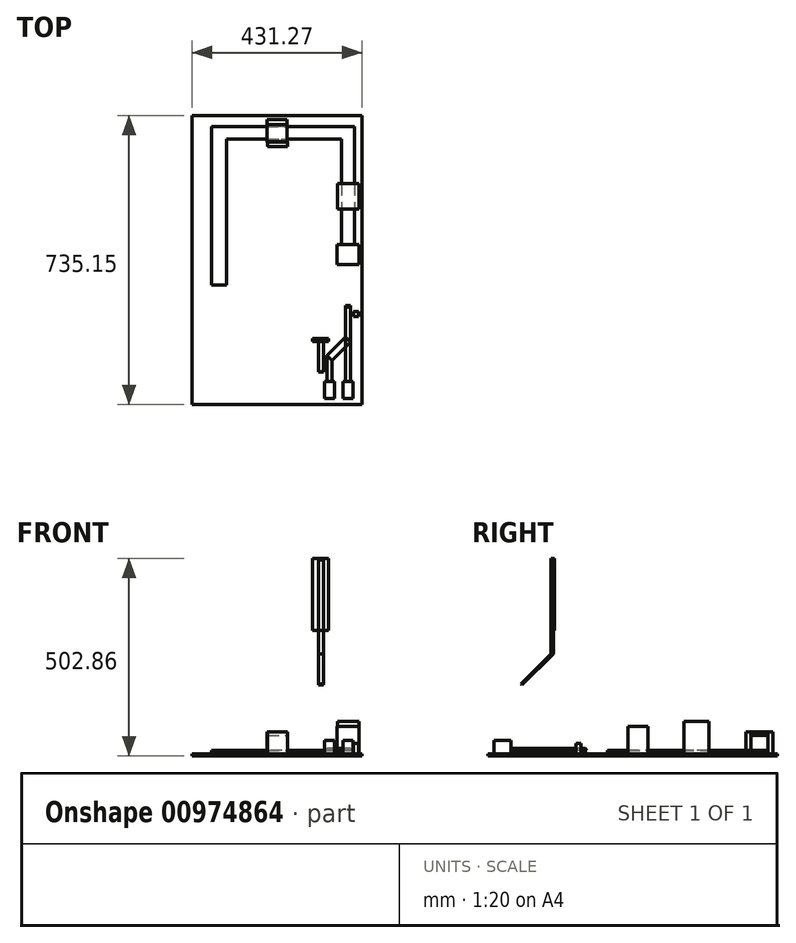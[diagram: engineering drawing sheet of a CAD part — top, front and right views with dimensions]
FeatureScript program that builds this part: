
annotation { "Feature Type Name" : "Feature", "Feature Type Description" : "" }
export const myFeature = defineFeature(function(context is Context, id is Id, definition is map)
    precondition{}
    {
        {
            var Q0;
            Q0=qCreatedBy(makeId("Top.planeOp"),FACE);
            var sketch = newSketch(context, id + "F0", { "sketchPlane" : qUnion([Q0])});
            skLineSegment(sketch, "E0.bottom", {"start": v(-24.86, -13.92) * mm, "end": v(0.54, -13.92) * mm});
            skLineSegment(sketch, "E0.top", {"start": v(-24.86, -57.1) * mm, "end": v(0.54, -57.1) * mm});
            skLineSegment(sketch, "E0.left", {"start": v(-24.86, -13.92) * mm, "end": v(-24.86, -57.1) * mm});
            skLineSegment(sketch, "E0.right", {"start": v(0.54, -13.92) * mm, "end": v(0.54, -57.1) * mm});
            skLineSegment(sketch, "E1.bottom", {"start": v(21.67, -13.98) * mm, "end": v(47.07, -13.98) * mm});
            skLineSegment(sketch, "E1.top", {"start": v(21.67, -57.16) * mm, "end": v(47.07, -57.16) * mm});
            skLineSegment(sketch, "E1.left", {"start": v(21.67, -13.98) * mm, "end": v(21.67, -57.16) * mm});
            skLineSegment(sketch, "E1.right", {"start": v(47.07, -13.98) * mm, "end": v(47.07, -57.16) * mm});
            skSolve(sketch);
        }
        {
            var Q0;
            Q0=qSketchRegion(id+"F0",true);
            extrude(context, id + "F1", {"entities" : qUnion([Q0]), "depth" : 34.3 * mm, "offsetDistance" : 25.4 * mm});
        }
        {
            var Q0;
            Q0=makeQuery(id+"F1.opExtrude","SWEPT_FACE",FACE,{"disambiguationData":[OSD([sQuery(id+"F0.wireOp",EDGE,"E1.bottom")])]});
            var sketch = newSketch(context, id + "F2", { "sketchPlane" : qUnion([Q0])});
            skLineSegment(sketch, "E2.bottom", {"start": v(-40.72, 13.97) * mm, "end": v(-28.02, 13.97) * mm});
            skLineSegment(sketch, "E2.top", {"start": v(-40.72, 9.52) * mm, "end": v(-28.02, 9.52) * mm});
            skLineSegment(sketch, "E2.left", {"start": v(-40.72, 13.97) * mm, "end": v(-40.72, 9.52) * mm});
            skLineSegment(sketch, "E2.right", {"start": v(-28.02, 13.97) * mm, "end": v(-28.02, 9.52) * mm});
            skLineSegment(sketch, "E3", {"start": v(-34.37, 9.52) * mm, "end": v(-34.37, 0) * mm});
            skLineSegment(sketch, "E4", {"start": v(-34.37, 13.97) * mm, "end": v(-34.37, 34.3) * mm});
            skLineSegment(sketch, "E5", {"start": v(-28.02, 11.75) * mm, "end": v(-21.67, 11.75) * mm});
            skSolve(sketch);
        }
        {
            var Q0;
            Q0=makeQuery(id+"F1.opExtrude","SWEPT_FACE",FACE,{"disambiguationData":[OSD([sQuery(id+"F0.wireOp",EDGE,"E0.bottom")])]});
            var sketch = newSketch(context, id + "F3", { "sketchPlane" : qUnion([Q0])});
            skLineSegment(sketch, "E6.bottom", {"start": v(5.8, 13.97) * mm, "end": v(18.5, 13.97) * mm});
            skLineSegment(sketch, "E6.top", {"start": v(5.8, 9.52) * mm, "end": v(18.5, 9.52) * mm});
            skLineSegment(sketch, "E6.left", {"start": v(5.8, 13.97) * mm, "end": v(5.8, 9.52) * mm});
            skLineSegment(sketch, "E6.right", {"start": v(18.5, 13.97) * mm, "end": v(18.5, 9.52) * mm});
            skLineSegment(sketch, "E7", {"start": v(12.16, 9.52) * mm, "end": v(12.16, 0) * mm});
            skLineSegment(sketch, "E8", {"start": v(12.16, 13.97) * mm, "end": v(12.16, 34.3) * mm});
            skLineSegment(sketch, "E9", {"start": v(18.5, 11.75) * mm, "end": v(24.86, 11.75) * mm});
            skSolve(sketch);
        }
        {
            var Q0;
            {var subQ4=sQuery(id+"F2.wireOp",EDGE,"E2.left");Q0=makeQuery(id+"F2.imprint","IMPRINT",FACE,{"disambiguationData":[TD([[makeQuery(id+"F2.imprint","IMPRINT",EDGE,{"derivedFrom":subQ4}),1.0]])]});}
            extrude(context, id + "F4", {"entities" : qUnion([Q0]), "operationType" : NewBodyOperationType.ADD, "depth" : 186.7 * mm, "offsetDistance" : 25.4 * mm});
        }
        {
            var Q0;
            {var subQ4=sQuery(id+"F3.wireOp",EDGE,"E6.left");Q0=makeQuery(id+"F3.imprint","IMPRINT",FACE,{"disambiguationData":[TD([[makeQuery(id+"F3.imprint","IMPRINT",EDGE,{"derivedFrom":subQ4}),1.0]])]});}
            extrude(context, id + "F5", {"entities" : qUnion([Q0]), "operationType" : NewBodyOperationType.ADD, "depth" : 66.04 * mm, "offsetDistance" : 25.4 * mm});
        }
        {
            var Q0;
            Q0=makeQuery(id+"F5.opExtrude","CAP_EDGE",EDGE,{"disambiguationData":[OSD([sQuery(id+"F3.wireOp",EDGE,"E6.left")])],"isStart":false});
            chamfer(context, id + "F6", {"entities" : qUnion([Q0]), "width" : 12.7 * mm, "tangentPropagation" : true});
        }
        {
            var Q0;
            Q0=makeQuery(id+"F6.opChamfer","BLEND_FACE",FACE,{"disambiguationData":[OSD([sQuery(id+"F3.wireOp",EDGE,"E6.left")])]});
            extrude(context, id + "F7", {"entities" : qUnion([Q0]), "depth" : 66.8 * mm, "offsetDistance" : 25.4 * mm});
        }
        {
            var Q0;
            Q0=qCreatedBy(makeId("Top.planeOp"),FACE);
            var sketch = newSketch(context, id + "F8", { "sketchPlane" : qUnion([Q0])});
            skLineSegment(sketch, "E10.bottom", {"start": v(49.17, 163.81) * mm, "end": v(61.08, 163.81) * mm});
            skLineSegment(sketch, "E10.top", {"start": v(49.17, 151.3) * mm, "end": v(61.08, 151.3) * mm});
            skLineSegment(sketch, "E10.left", {"start": v(49.17, 163.81) * mm, "end": v(49.17, 151.3) * mm});
            skLineSegment(sketch, "E10.right", {"start": v(61.08, 163.81) * mm, "end": v(61.08, 151.3) * mm});
            skSolve(sketch);
        }
        {
            var Q0;
            Q0=makeQuery(id+"F8.imprint","IMPRINT",FACE,{"disambiguationData":[TD([[makeQuery(id+"F8.imprint","IMPRINT",EDGE,{"derivedFrom":sQuery(id+"F8.wireOp",EDGE,"E10.bottom")}),-1.0]])]});
            extrude(context, id + "F9", {"entities" : qUnion([Q0]), "depth" : 27.18 * mm, "offsetDistance" : 25.4 * mm});
        }
        {
            var Q0;
            Q0=makeQuery(id+"F4.opExtrude","CAP_FACE",FACE,{"disambiguationData":[OSD([sQuery(id+"F2.wireOp",EDGE,"E2.bottom"),sQuery(id+"F2.wireOp",EDGE,"E2.top"),sQuery(id+"F2.wireOp",EDGE,"E2.left"),sQuery(id+"F2.wireOp",EDGE,"E2.right")])],"isStart":false});
            extrude(context, id + "F10", {"entities" : qUnion([Q0]), "operationType" : NewBodyOperationType.ADD, "depth" : 7.62 * mm, "offsetDistance" : 25.4 * mm});
        }
        {
            var Q0;
            Q0=makeQuery(id+"F10.opExtrude","CAP_EDGE",EDGE,{"disambiguationData":[OSD([sQuery(id+"F2.wireOp",EDGE,"E2.bottom")])],"isStart":false});
            chamfer(context, id + "F11", {"entities" : qUnion([Q0]), "width" : 5.08 * mm, "tangentPropagation" : true});
        }
        {
            var Q0;
            Q0=makeQuery(id+"F11.opChamfer","BLEND_FACE",FACE,{"disambiguationData":[OSD([sQuery(id+"F2.wireOp",EDGE,"E2.bottom")])]});
            var sketch = newSketch(context, id + "F12", { "sketchPlane" : qUnion([Q0])});
            skLineSegment(sketch, "E11.bottom", {"start": v(40.72, 114.04) * mm, "end": v(28.02, 114.04) * mm});
            skLineSegment(sketch, "E11.top", {"start": v(40.72, 117.9) * mm, "end": v(28.02, 117.9) * mm});
            skLineSegment(sketch, "E11.left", {"start": v(40.72, 114.04) * mm, "end": v(40.72, 117.9) * mm});
            skLineSegment(sketch, "E11.right", {"start": v(28.02, 114.04) * mm, "end": v(28.02, 117.9) * mm});
            skSolve(sketch);
        }
        {
            var Q0;
            Q0=makeQuery(id+"F12.imprint","IMPRINT",FACE,{"disambiguationData":[TD([[makeQuery(id+"F12.imprint","IMPRINT",EDGE,{"derivedFrom":sQuery(id+"F12.wireOp",EDGE,"E11.bottom")}),-1.0]])]});
            extrude(context, id + "F13", {"entities" : qUnion([Q0]), "operationType" : NewBodyOperationType.ADD, "depth" : 114.3 * mm, "offsetDistance" : 25.4 * mm});
        }
        {
            var Q0;
            Q0=makeQuery(id+"F13.opExtrude","CAP_EDGE",EDGE,{"disambiguationData":[OSD([sQuery(id+"F12.wireOp",EDGE,"E11.top")])],"isStart":false});
            chamfer(context, id + "F14", {"entities" : qUnion([Q0]), "width" : 5.08 * mm, "tangentPropagation" : true});
        }
        {
            var Q0;
            Q0=makeQuery(id+"F14.opChamfer","BLEND_FACE",FACE,{"disambiguationData":[OSD([sQuery(id+"F12.wireOp",EDGE,"E11.top")])]});
            extrude(context, id + "F15", {"entities" : qUnion([Q0]), "operationType" : NewBodyOperationType.ADD, "depth" : 59.18 * mm, "offsetDistance" : 25.4 * mm});
        }
        {
            var Q0;
            Q0=qCreatedBy(makeId("Top.planeOp"),FACE);
            var sketch = newSketch(context, id + "F16", { "sketchPlane" : qUnion([Q0])});
            skLineSegment(sketch, "E12.bottom", {"start": v(7.08, 334.15) * mm, "end": v(62.96, 334.15) * mm});
            skLineSegment(sketch, "E12.top", {"start": v(7.08, 283.35) * mm, "end": v(62.96, 283.35) * mm});
            skLineSegment(sketch, "E12.left", {"start": v(7.08, 334.15) * mm, "end": v(7.08, 283.35) * mm});
            skLineSegment(sketch, "E12.right", {"start": v(62.96, 334.15) * mm, "end": v(62.96, 283.35) * mm});
            skSolve(sketch);
        }
        {
            var Q0;
            Q0=makeQuery(id+"F16.imprint","IMPRINT",FACE,{"disambiguationData":[TD([[makeQuery(id+"F16.imprint","IMPRINT",EDGE,{"derivedFrom":sQuery(id+"F16.wireOp",EDGE,"E12.bottom")}),-1.0]])]});
            extrude(context, id + "F17", {"entities" : qUnion([Q0]), "depth" : 69.85 * mm, "offsetDistance" : 25.4 * mm});
        }
        {
            var Q0;
            Q0=makeQuery(id+"F17.opExtrude","SWEPT_FACE",FACE,{"disambiguationData":[OSD([sQuery(id+"F16.wireOp",EDGE,"E12.bottom")])]});
            var sketch = newSketch(context, id + "F18", { "sketchPlane" : qUnion([Q0])});
            skLineSegment(sketch, "E13.bottom", {"start": v(-51.53, 0) * mm, "end": v(-18.51, 0) * mm});
            skLineSegment(sketch, "E13.top", {"start": v(-51.53, 9.8) * mm, "end": v(-18.51, 9.8) * mm});
            skLineSegment(sketch, "E13.left", {"start": v(-51.53, 0) * mm, "end": v(-51.53, 9.8) * mm});
            skLineSegment(sketch, "E13.right", {"start": v(-18.51, 0) * mm, "end": v(-18.51, 9.8) * mm});
            skLineSegment(sketch, "E14", {"start": v(-18.51, 4.9) * mm, "end": v(-7.08, 4.9) * mm});
            skLineSegment(sketch, "E15", {"start": v(-51.53, 4.9) * mm, "end": v(-62.96, 4.9) * mm});
            skSolve(sketch);
        }
        {
            var Q0;
            {var subQ3=sQuery(id+"F18.wireOp",EDGE,"E13.bottom");Q0=makeQuery(id+"F18.imprint","IMPRINT",FACE,{"disambiguationData":[TD([[makeQuery(id+"F18.imprint","IMPRINT",EDGE,{"derivedFrom":subQ3}),-1.0]])]});}
            extrude(context, id + "F19", {"entities" : qUnion([Q0]), "operationType" : NewBodyOperationType.ADD, "depth" : 91.19 * mm, "offsetDistance" : 25.4 * mm});
        }
        {
            var Q0;
            Q0=makeQuery(id+"F19.opExtrude","CAP_FACE",FACE,{"disambiguationData":[OSD([sQuery(id+"F18.wireOp",EDGE,"E13.bottom"),sQuery(id+"F18.wireOp",EDGE,"E13.top"),sQuery(id+"F18.wireOp",EDGE,"E13.left"),sQuery(id+"F18.wireOp",EDGE,"E13.right")])],"isStart":false});
            var sketch = newSketch(context, id + "F20", { "sketchPlane" : qUnion([Q0])});
            skLineSegment(sketch, "E16.bottom", {"start": v(-62.7, 83.36) * mm, "end": v(-7.85, 83.36) * mm});
            skLineSegment(sketch, "E16.top", {"start": v(-62.7, 0) * mm, "end": v(-7.85, 0) * mm});
            skLineSegment(sketch, "E16.left", {"start": v(-62.7, 83.36) * mm, "end": v(-62.7, 0) * mm});
            skLineSegment(sketch, "E16.right", {"start": v(-7.85, 83.36) * mm, "end": v(-7.85, 0) * mm});
            skSolve(sketch);
        }
        {
            var Q0;
            Q0=makeQuery(id+"F20.imprint","IMPRINT",FACE,{"disambiguationData":[TD([[makeQuery(id+"F20.imprint","IMPRINT",EDGE,{"derivedFrom":sQuery(id+"F20.wireOp",EDGE,"E16.bottom")}),-1.0]])]});
            extrude(context, id + "F21", {"entities" : qUnion([Q0]), "depth" : 63.75 * mm, "offsetDistance" : 25.4 * mm});
        }
        {
            var Q0;
            Q0=makeQuery(id+"F19.opExtrude","CAP_FACE",FACE,{"disambiguationData":[OSD([sQuery(id+"F18.wireOp",EDGE,"E13.bottom"),sQuery(id+"F18.wireOp",EDGE,"E13.top"),sQuery(id+"F18.wireOp",EDGE,"E13.left"),sQuery(id+"F18.wireOp",EDGE,"E13.right")])],"isStart":false});
            extrude(context, id + "F22", {"entities" : qUnion([Q0]), "depth" : 208.79 * mm, "offsetDistance" : 25.4 * mm});
        }
        {
            var Q0;
            Q0=makeQuery(id+"F15.opExtrude","CAP_FACE",FACE,{"disambiguationData":[OSD([sQuery(id+"F12.wireOp",EDGE,"E11.top")])],"isStart":false});
            var sketch = newSketch(context, id + "F23", { "sketchPlane" : qUnion([Q0])});
            skLineSegment(sketch, "E17.bottom", {"start": v(-55.51, 96.22) * mm, "end": v(-15.14, 96.22) * mm});
            skLineSegment(sketch, "E17.top", {"start": v(-55.51, 88.46) * mm, "end": v(-15.14, 88.46) * mm});
            skLineSegment(sketch, "E17.left", {"start": v(-55.51, 96.22) * mm, "end": v(-55.51, 88.46) * mm});
            skLineSegment(sketch, "E17.right", {"start": v(-15.14, 96.22) * mm, "end": v(-15.14, 88.46) * mm});
            skSolve(sketch);
        }
        {
            var Q0;
            Q0=makeQuery(id+"F23.imprint","IMPRINT",FACE,{"disambiguationData":[TD([[makeQuery(id+"F23.imprint","IMPRINT",EDGE,{"derivedFrom":sQuery(id+"F23.wireOp",EDGE,"E17.bottom")}),-1.0]])]});
            extrude(context, id + "F24", {"entities" : qUnion([Q0]), "depth" : 183.39 * mm, "offsetDistance" : 25.4 * mm});
        }
        {
            var Q0;
            Q0=makeQuery(id+"F15.opExtrude","CAP_FACE",FACE,{"disambiguationData":[OSD([sQuery(id+"F12.wireOp",EDGE,"E11.top")])],"isStart":false});
            extrude(context, id + "F25", {"entities" : qUnion([Q0]), "depth" : 179.07 * mm, "offsetDistance" : 25.4 * mm});
        }
        {
            var Q0;
            Q0=makeQuery(id+"F22.opExtrude","SWEPT_FACE",FACE,{"disambiguationData":[OSD([sQuery(id+"F18.wireOp",EDGE,"E13.right")])]});
            var sketch = newSketch(context, id + "F26", { "sketchPlane" : qUnion([Q0])});
            skLineSegment(sketch, "E18.bottom", {"start": v(-634.12, 9.8) * mm, "end": v(-602.75, 9.8) * mm});
            skLineSegment(sketch, "E18.top", {"start": v(-634.12, 0) * mm, "end": v(-602.75, 0) * mm});
            skLineSegment(sketch, "E18.left", {"start": v(-634.12, 9.8) * mm, "end": v(-634.12, 0) * mm});
            skLineSegment(sketch, "E18.right", {"start": v(-602.75, 9.8) * mm, "end": v(-602.75, 0) * mm});
            skSolve(sketch);
        }
        {
            var Q0;
            Q0=makeQuery(id+"F26.imprint","IMPRINT",FACE,{"disambiguationData":[TD([[makeQuery(id+"F26.imprint","IMPRINT",EDGE,{"derivedFrom":sQuery(id+"F26.wireOp",EDGE,"E18.bottom")}),-1.0]])]});
            extrude(context, id + "F27", {"entities" : qUnion([Q0]), "operationType" : NewBodyOperationType.ADD, "depth" : 271.78 * mm, "offsetDistance" : 25.4 * mm});
        }
        {
            var Q0;
            Q0=makeQuery(id+"F27.opExtrude","CAP_FACE",FACE,{"disambiguationData":[OSD([sQuery(id+"F26.wireOp",EDGE,"E18.bottom"),sQuery(id+"F26.wireOp",EDGE,"E18.top"),sQuery(id+"F26.wireOp",EDGE,"E18.left"),sQuery(id+"F26.wireOp",EDGE,"E18.right")])],"isStart":false});
            extrude(context, id + "F28", {"entities" : qUnion([Q0]), "operationType" : NewBodyOperationType.ADD, "depth" : 58.17 * mm, "offsetDistance" : 25.4 * mm});
        }
        {
            var Q0;
            {var subQ0=sQuery(id+"F26.wireOp",EDGE,"E18.right");Q0=makeQuery(id+"F28.boolean.opBoolean","MERGE",FACE,{"derivedFrom":[makeQuery(id+"F27.opExtrude","SWEPT_FACE",FACE,{"disambiguationData":[OSD([subQ0])]}),makeQuery(id+"F28.opExtrude","SWEPT_FACE",FACE,{"disambiguationData":[OSD([subQ0])]})]});}
            var sketch = newSketch(context, id + "F29", { "sketchPlane" : qUnion([Q0])});
            skLineSegment(sketch, "E19.bottom", {"start": v(-311.43, 9.8) * mm, "end": v(-273.29, 9.8) * mm});
            skLineSegment(sketch, "E19.top", {"start": v(-311.43, 0) * mm, "end": v(-273.29, 0) * mm});
            skLineSegment(sketch, "E19.left", {"start": v(-311.43, 9.8) * mm, "end": v(-311.43, 0) * mm});
            skLineSegment(sketch, "E19.right", {"start": v(-273.29, 9.8) * mm, "end": v(-273.29, 0) * mm});
            skSolve(sketch);
        }
        {
            var Q0;
            Q0=makeQuery(id+"F29.imprint","IMPRINT",FACE,{"disambiguationData":[TD([[makeQuery(id+"F29.imprint","IMPRINT",EDGE,{"derivedFrom":sQuery(id+"F29.wireOp",EDGE,"E19.bottom")}),-1.0]])]});
            extrude(context, id + "F30", {"entities" : qUnion([Q0]), "operationType" : NewBodyOperationType.ADD, "depth" : 370.84 * mm, "offsetDistance" : 25.4 * mm});
        }
        {
            var Q0;
            Q0=qCreatedBy(makeId("Top.planeOp"),FACE);
            var sketch = newSketch(context, id + "F31", { "sketchPlane" : qUnion([Q0])});
            skLineSegment(sketch, "E20.bottom", {"start": v(-170.62, 639.51) * mm, "end": v(-119.82, 639.51) * mm});
            skLineSegment(sketch, "E20.top", {"start": v(-170.62, 652.21) * mm, "end": v(-119.82, 652.21) * mm});
            skLineSegment(sketch, "E20.left", {"start": v(-170.62, 639.51) * mm, "end": v(-170.62, 652.21) * mm});
            skLineSegment(sketch, "E20.right", {"start": v(-119.82, 639.51) * mm, "end": v(-119.82, 652.21) * mm});
            skLineSegment(sketch, "E21.bottom", {"start": v(-169.98, 583.7) * mm, "end": v(-119.18, 583.7) * mm});
            skLineSegment(sketch, "E21.top", {"start": v(-169.98, 596.4) * mm, "end": v(-119.18, 596.4) * mm});
            skLineSegment(sketch, "E21.left", {"start": v(-169.98, 583.7) * mm, "end": v(-169.98, 596.4) * mm});
            skLineSegment(sketch, "E21.right", {"start": v(-119.18, 583.7) * mm, "end": v(-119.18, 596.4) * mm});
            skLineSegment(sketch, "E22", {"start": v(-119.82, 639.51) * mm, "end": v(-119.18, 596.4) * mm});
            skLineSegment(sketch, "E23", {"start": v(-169.98, 596.4) * mm, "end": v(-170.62, 639.51) * mm});
            skSolve(sketch);
        }
        {
            var Q0;
            Q0=makeQuery(id+"F31.imprint","IMPRINT",FACE,{"disambiguationData":[TD([[makeQuery(id+"F31.imprint","IMPRINT",EDGE,{"derivedFrom":sQuery(id+"F31.wireOp",EDGE,"E20.bottom")}),1.0]])]});
            var Q1;
            Q1=makeQuery(id+"F31.imprint","IMPRINT",FACE,{"disambiguationData":[TD([[makeQuery(id+"F31.imprint","IMPRINT",EDGE,{"derivedFrom":sQuery(id+"F31.wireOp",EDGE,"E21.bottom")}),1.0]])]});
            extrude(context, id + "F32", {"entities" : qUnion([Q0, Q1]), "depth" : 55.88 * mm, "offsetDistance" : 25.4 * mm});
        }
        {
            var Q0;
            Q0=makeQuery(id+"F32.opExtrude","SWEPT_FACE",FACE,{"disambiguationData":[OSD([sQuery(id+"F31.wireOp",EDGE,"E20.bottom")])]});
            var sketch = newSketch(context, id + "F33", { "sketchPlane" : qUnion([Q0])});
            skLineSegment(sketch, "E24.bottom", {"start": v(-170.62, 55.88) * mm, "end": v(-119.82, 55.88) * mm});
            skLineSegment(sketch, "E24.top", {"start": v(-170.62, 47.74) * mm, "end": v(-119.82, 47.74) * mm});
            skLineSegment(sketch, "E24.left", {"start": v(-170.62, 55.88) * mm, "end": v(-170.62, 47.74) * mm});
            skLineSegment(sketch, "E24.right", {"start": v(-119.82, 55.88) * mm, "end": v(-119.82, 47.74) * mm});
            skSolve(sketch);
        }
        {
            var Q0;
            Q0=makeQuery(id+"F33.imprint","IMPRINT",FACE,{"disambiguationData":[TD([[makeQuery(id+"F33.imprint","IMPRINT",EDGE,{"derivedFrom":sQuery(id+"F33.wireOp",EDGE,"E24.bottom")}),-1.0]])]});
            extrude(context, id + "F34", {"entities" : qUnion([Q0]), "depth" : 44.7 * mm, "offsetDistance" : 25.4 * mm});
        }
        {
            var Q0;
            Q0=qCreatedBy(makeId("Top.planeOp"),FACE);
            var sketch = newSketch(context, id + "F35", { "sketchPlane" : qUnion([Q0])});
            skLineSegment(sketch, "E25.bottom", {"start": v(-361.05, 662.81) * mm, "end": v(70.22, 662.81) * mm});
            skLineSegment(sketch, "E25.top", {"start": v(-361.05, -72.34) * mm, "end": v(70.22, -72.34) * mm});
            skLineSegment(sketch, "E25.left", {"start": v(-361.05, 662.81) * mm, "end": v(-361.05, -72.34) * mm});
            skLineSegment(sketch, "E25.right", {"start": v(70.22, 662.81) * mm, "end": v(70.22, -72.34) * mm});
            skSolve(sketch);
        }
        {
            var Q0;
            Q0=makeQuery(id+"F35.imprint","IMPRINT",FACE,{"disambiguationData":[TD([[makeQuery(id+"F35.imprint","IMPRINT",EDGE,{"derivedFrom":sQuery(id+"F35.wireOp",EDGE,"E25.bottom")}),-1.0]])]});
            extrude(context, id + "F36", {"entities" : qUnion([Q0]), "depth" : -5.08 * mm, "offsetDistance" : 25.4 * mm});
        }
    });
